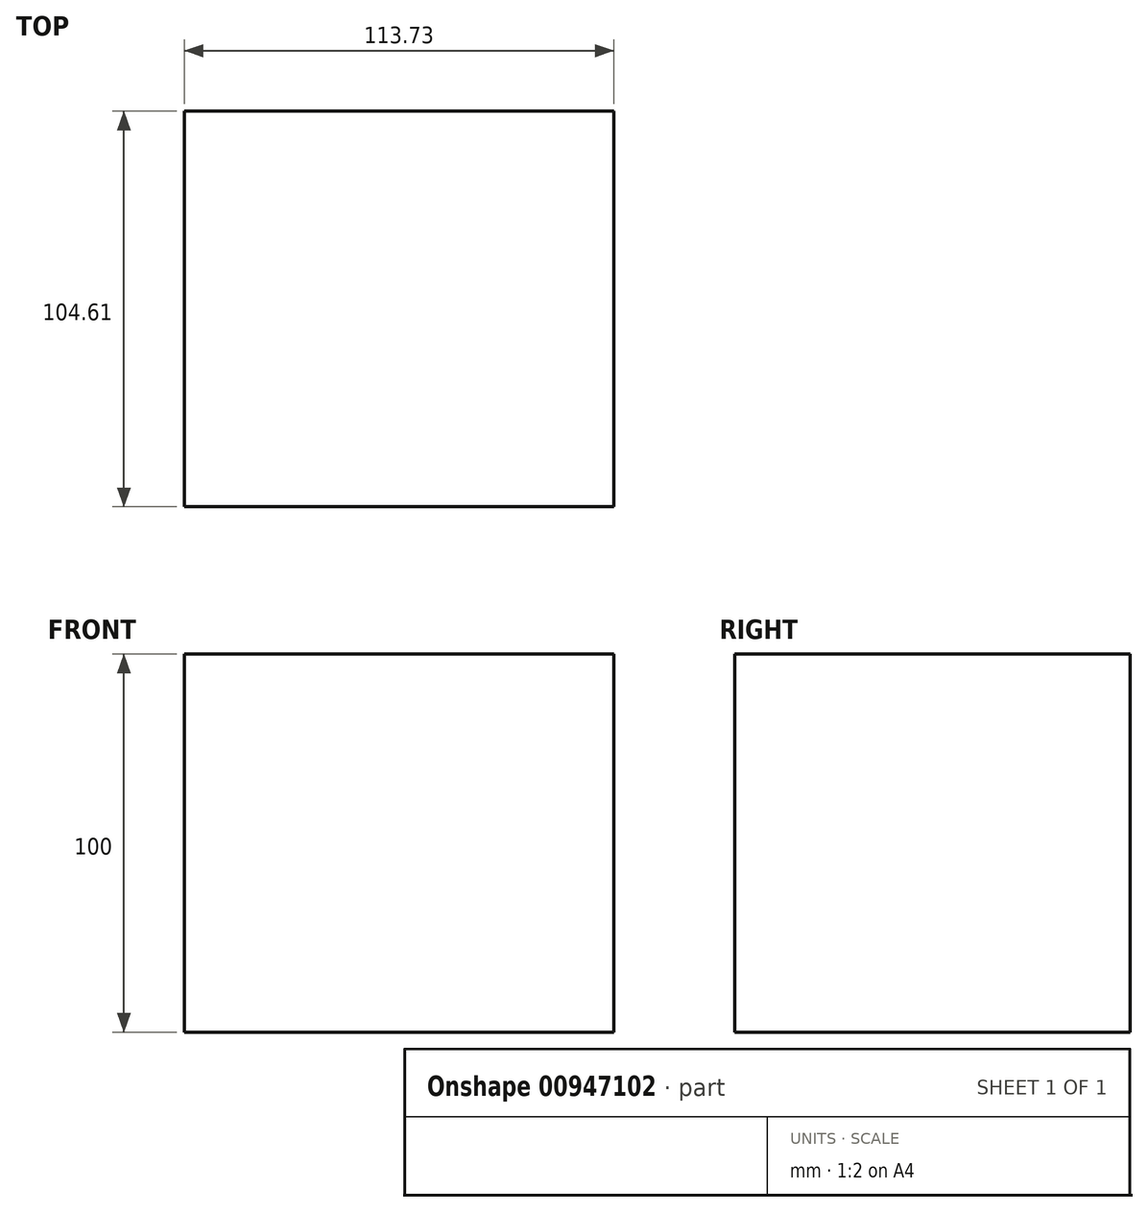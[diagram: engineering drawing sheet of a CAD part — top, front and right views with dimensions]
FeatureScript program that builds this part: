
annotation { "Feature Type Name" : "Feature", "Feature Type Description" : "" }
export const myFeature = defineFeature(function(context is Context, id is Id, definition is map)
    precondition{}
    {
        {
            var Q0;
            Q0=qCreatedBy(makeId("Top.planeOp"),FACE);
            var sketch = newSketch(context, id + "F0", { "sketchPlane" : qUnion([Q0])});
            skLineSegment(sketch, "E0.bottom", {"start": v(-54.68, -55.48) * mm, "end": v(59.05, -55.48) * mm});
            skLineSegment(sketch, "E0.top", {"start": v(-54.68, 49.13) * mm, "end": v(59.05, 49.13) * mm});
            skLineSegment(sketch, "E0.left", {"start": v(-54.68, 49.13) * mm, "end": v(-54.68, -55.48) * mm});
            skLineSegment(sketch, "E0.right", {"start": v(59.05, 49.13) * mm, "end": v(59.05, -55.48) * mm});
            skSolve(sketch);
        }
        {
            var Q0;
            Q0 = qSketchRegion(id + "F0", true);
            extrude(context, id + "F1", {"entities" : qUnion([Q0]), "endBound" : BoundingType.SYMMETRIC, "depth" : 100 * mm, "offsetDistance" : 25 * mm});
        }
    });
